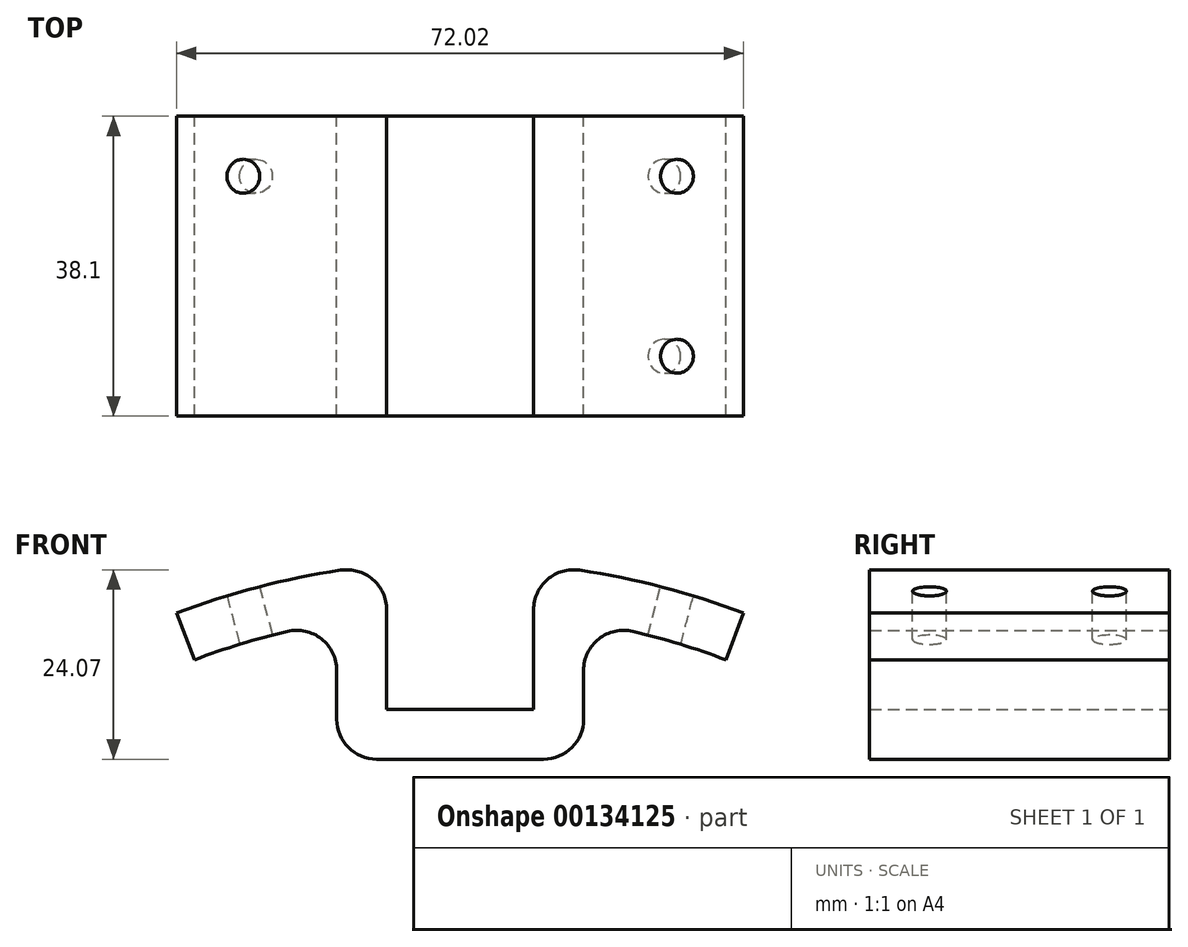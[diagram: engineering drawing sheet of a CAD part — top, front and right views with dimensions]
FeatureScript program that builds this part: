
annotation { "Feature Type Name" : "Feature", "Feature Type Description" : "" }
export const myFeature = defineFeature(function(context is Context, id is Id, definition is map)
    precondition{}
    {
        {
            var Q0;
            Q0=qCreatedBy(makeId("Front.planeOp"),FACE);
            var sketch = newSketch(context, id + "F0", { "sketchPlane" : qUnion([Q0])});
            skArc(sketch, "E0", {"start": v(-9.33, 101.17) * mm, "mid": v(-22.88, 99) * mm, "end": v(-36, 95) * mm});
            skLineSegment(sketch, "E1.bottom", {"start": v(9.33, 82.8) * mm, "end": v(-9.33, 82.8) * mm});
            skLineSegment(sketch, "E1.left", {"start": v(9.33, 82.8) * mm, "end": v(9.33, 101.17) * mm});
            skLineSegment(sketch, "E1.right", {"start": v(-9.33, 82.8) * mm, "end": v(-9.33, 101.17) * mm});
            skPoint(sketch, "E1.middle", {"position": v(0, 101.6) * mm});
            skArc(sketch, "E2", {"start": v(-15.68, 93.95) * mm, "mid": v(-24.84, 91.95) * mm, "end": v(-33.76, 89.07) * mm});
            skPoint(sketch, "E3.orphan", {"position": v(9.33, 120.4) * mm});
            skPoint(sketch, "E4.orphan", {"position": v(-9.33, 120.4) * mm});
            skLineSegment(sketch, "E5.bottom", {"start": v(15.68, 76.45) * mm, "end": v(-15.68, 76.45) * mm});
            skLineSegment(sketch, "E5.left", {"start": v(15.68, 76.45) * mm, "end": v(15.68, 93.95) * mm});
            skLineSegment(sketch, "E5.right", {"start": v(-15.68, 76.45) * mm, "end": v(-15.68, 93.95) * mm});
            skPoint(sketch, "E6.MirrorCS.end.orphan", {"position": v(27.3, 97.87) * mm});
            skPoint(sketch, "E7.end.orphan", {"position": v(-27.3, 97.87) * mm});
            skPoint(sketch, "E5.top.start.orphan", {"position": v(15.68, 126.75) * mm});
            skPoint(sketch, "E8.orphan", {"position": v(-15.68, 126.75) * mm});
            skLineSegment(sketch, "E9", {"start": v(-33.76, 89.07) * mm, "end": v(-36, 95) * mm});
            skLineSegment(sketch, "E10.MirrorCS", {"start": v(33.76, 89.07) * mm, "end": v(36, 95) * mm});
            skArc(sketch, "E11.trimOffspring", {"start": v(36, 95) * mm, "mid": v(22.88, 99) * mm, "end": v(9.33, 101.17) * mm});
            skArc(sketch, "E12.trimOffspring", {"start": v(33.76, 89.07) * mm, "mid": v(24.84, 91.95) * mm, "end": v(15.68, 93.95) * mm});
            skSolve(sketch);
        }
        {
            var Q0;
            Q0=makeQuery(id+"F0.imprint","IMPRINT",FACE,{"disambiguationData":[TD([[makeQuery(id+"F0.imprint","IMPRINT",EDGE,{"derivedFrom":sQuery(id+"F0.wireOp",EDGE,"E0")}),1.0]])]});
            extrude(context, id + "F1", {"entities" : qUnion([Q0]), "depth" : 38.1 * mm});
        }
        {
            var Q0;
            Q0=makeQuery(id+"F1.opExtrude","SWEPT_EDGE",EDGE,{"disambiguationData":[OSD([sQuery(id+"F0.wireOp",EDGE,"E0"),sQuery(id+"F0.wireOp",EDGE,"E1.right")])]});
            var Q1;
            Q1=makeQuery(id+"F1.opExtrude","SWEPT_EDGE",EDGE,{"disambiguationData":[OSD([sQuery(id+"F0.wireOp",EDGE,"E1.left"),sQuery(id+"F0.wireOp",EDGE,"E11.trimOffspring")])]});
            var Q2;
            Q2=makeQuery(id+"F1.opExtrude","SWEPT_EDGE",EDGE,{"disambiguationData":[OSD([sQuery(id+"F0.wireOp",EDGE,"E5.left"),sQuery(id+"F0.wireOp",EDGE,"E12.trimOffspring")])]});
            var Q3;
            Q3=makeQuery(id+"F1.opExtrude","SWEPT_EDGE",EDGE,{"disambiguationData":[OSD([sQuery(id+"F0.wireOp",EDGE,"E2"),sQuery(id+"F0.wireOp",EDGE,"E5.right")])]});
            var Q4;
            Q4=makeQuery(id+"F1.opExtrude","SWEPT_EDGE",EDGE,{"disambiguationData":[OSD([sQuery(id+"F0.wireOp",EDGE,"E5.bottom"),sQuery(id+"F0.wireOp",EDGE,"E5.left")])]});
            var Q5;
            Q5=makeQuery(id+"F1.opExtrude","SWEPT_EDGE",EDGE,{"disambiguationData":[OSD([sQuery(id+"F0.wireOp",EDGE,"E5.bottom"),sQuery(id+"F0.wireOp",EDGE,"E5.right")])]});
            fillet(context, id + "F2", {"entities" : qUnion([Q0, Q1, Q2, Q3, Q4, Q5]), "radius" : 5.08 * mm, "tangentPropagation" : true, "allowEdgeOverflow" : false});
        }
        {
            var Q0;
            Q0=makeQuery(id+"F1.opExtrude","SWEPT_EDGE",EDGE,{"disambiguationData":[OSD([sQuery(id+"F0.wireOp",EDGE,"E0"),sQuery(id+"F0.wireOp",EDGE,"E9")])]});
            var Q1;
            {var subQ0=sQuery(id+"F0.wireOp",EDGE,"E0");Q1=makeQuery(id+"F2.opFillet","BLEND_EDGE",EDGE,{"blendedFrom":[makeQuery(id+"F1.opExtrude","SWEPT_EDGE",EDGE,{"disambiguationData":[OSD([subQ0,sQuery(id+"F0.wireOp",EDGE,"E1.right")])]}),makeQuery(id+"F1.opExtrude","SWEPT_FACE",FACE,{"disambiguationData":[OSD([subQ0])]})],"blendedInto":[makeQuery(id+"F1.opExtrude","SWEPT_FACE",FACE,{"disambiguationData":[OSD([subQ0])]})]});}
            cPlane(context, id + "F3", {"entities" : qUnion([Q0, Q1]), "cplaneType" : CPlaneType.LINE_ANGLE, "offset" : 25.4 * mm, "angle" : 0 * degree, "width" : 152.4 * mm, "height" : 152.4 * mm});
        }
        {
            var Q0;
            Q0=qCreatedBy(id+"F3.planeOp",FACE);
            var sketch = newSketch(context, id + "F4", { "sketchPlane" : qUnion([Q0])});
            skCircle(sketch, "E13", {"center": v(-1.88, 7.62) * mm, "radius": 2.16 * mm});
            skLineSegment(sketch, "E14", {"start": v(-1.88, 0) * mm, "end": v(-10.77, 0) * mm});
            skLineSegment(sketch, "E15", {"start": v(-1.88, 38.1) * mm, "end": v(-10.77, 38.1) * mm});
            skLineSegment(sketch, "E16", {"start": v(-1.88, 38.1) * mm, "end": v(-1.88, 0) * mm});
            skCircle(sketch, "E17", {"center": v(-1.88, 30.48) * mm, "radius": 2.16 * mm});
            skLineSegment(sketch, "E18", {"start": v(-1.88, 38.1) * mm, "end": v(-1.88, 30.48) * mm});
            skSolve(sketch);
        }
        {
            var Q0;
            {var subQ0=sQuery(id+"F0.wireOp",EDGE,"E11.trimOffspring");Q0=makeQuery(id+"F2.opFillet","BLEND_EDGE",EDGE,{"blendedFrom":[makeQuery(id+"F1.opExtrude","SWEPT_EDGE",EDGE,{"disambiguationData":[OSD([sQuery(id+"F0.wireOp",EDGE,"E1.left"),subQ0])]}),makeQuery(id+"F1.opExtrude","SWEPT_FACE",FACE,{"disambiguationData":[OSD([subQ0])]})],"blendedInto":[makeQuery(id+"F1.opExtrude","SWEPT_FACE",FACE,{"disambiguationData":[OSD([subQ0])]})]});}
            var Q1;
            Q1=makeQuery(id+"F1.opExtrude","SWEPT_EDGE",EDGE,{"disambiguationData":[OSD([sQuery(id+"F0.wireOp",EDGE,"E10.MirrorCS"),sQuery(id+"F0.wireOp",EDGE,"E11.trimOffspring")])]});
            cPlane(context, id + "F5", {"entities" : qUnion([Q0, Q1]), "cplaneType" : CPlaneType.LINE_ANGLE, "offset" : 25.4 * mm, "angle" : 0 * degree, "width" : 152.4 * mm, "height" : 152.4 * mm});
        }
        {
            var Q0;
            Q0=qCreatedBy(id+"F5.planeOp",FACE);
            var sketch = newSketch(context, id + "F6", { "sketchPlane" : qUnion([Q0])});
            skCircle(sketch, "E19", {"center": v(1.88, 7.62) * mm, "radius": 2.16 * mm});
            skCircle(sketch, "E20", {"center": v(1.88, 30.48) * mm, "radius": 2.16 * mm});
            skLineSegment(sketch, "E21", {"start": v(10.77, 38.1) * mm, "end": v(1.88, 38.1) * mm});
            skLineSegment(sketch, "E22", {"start": v(1.88, 0) * mm, "end": v(10.77, 0) * mm});
            skLineSegment(sketch, "E23", {"start": v(1.88, 0) * mm, "end": v(1.88, 38.1) * mm});
            skSolve(sketch);
        }
        {
            var Q0;
            {var subQ0=sQuery(id+"F4.wireOp",EDGE,"E13");var subQ1=sQuery(id+"F4.wireOp",EDGE,"MtRigjMj-3dSd-aA1d-ol25-ydxgadoNVgCU");var subQ2=makeQuery(id+"F4.imprint","INTERSECT",VERTEX,{"disambiguationData":[OD(0.0)],"derivedFrom":[subQ1,subQ0]});Q0=makeQuery(id+"F4.imprint","IMPRINT",FACE,{"disambiguationData":[TD([[makeQuery(id+"F4.imprint","IMPRINT",EDGE,{"disambiguationData":[TD([[subQ2,1.0]])],"derivedFrom":subQ1}),1.0]])]});}
            var Q1;
            {var subQ0=sQuery(id+"F4.wireOp",EDGE,"E13");var subQ1=sQuery(id+"F4.wireOp",EDGE,"MtRigjMj-3dSd-aA1d-ol25-ydxgadoNVgCU");var subQ2=makeQuery(id+"F4.imprint","INTERSECT",VERTEX,{"disambiguationData":[OD(0.0)],"derivedFrom":[subQ1,subQ0]});Q1=makeQuery(id+"F4.imprint","IMPRINT",FACE,{"disambiguationData":[TD([[makeQuery(id+"F4.imprint","IMPRINT",EDGE,{"disambiguationData":[TD([[subQ2,1.0]])],"derivedFrom":subQ1}),-1.0]])]});}
            var Q2;
            Q2=makeQuery(id+"F4.imprint","IMPRINT",FACE,{"disambiguationData":[TD([[makeQuery(id+"F4.imprint","IMPRINT",EDGE,{"derivedFrom":sQuery(id+"F4.wireOp",EDGE,"FilW5u5A-EfiJ-iQZp-4yOM-Yht80zadNHdD")}),1.0]])]});
            var Q3;
            {var subQ0=sQuery(id+"F6.wireOp",EDGE,"AlFrU4an-jmT9-QRRX-vHQV-c8fI0KjrH0Lw");var subQ1=sQuery(id+"F6.wireOp",EDGE,"E20");var subQ2=makeQuery(id+"F6.imprint","INTERSECT",VERTEX,{"disambiguationData":[OD(0.0)],"derivedFrom":[subQ1,subQ0]});Q3=makeQuery(id+"F6.imprint","IMPRINT",FACE,{"disambiguationData":[TD([[makeQuery(id+"F6.imprint","IMPRINT",EDGE,{"disambiguationData":[TD([[subQ2,-1.0]])],"derivedFrom":subQ1}),1.0]])]});}
            var Q4;
            {var subQ0=sQuery(id+"F6.wireOp",EDGE,"AlFrU4an-jmT9-QRRX-vHQV-c8fI0KjrH0Lw");var subQ1=sQuery(id+"F6.wireOp",EDGE,"E20");var subQ2=makeQuery(id+"F6.imprint","INTERSECT",VERTEX,{"disambiguationData":[OD(0.0)],"derivedFrom":[subQ1,subQ0]});Q4=makeQuery(id+"F6.imprint","IMPRINT",FACE,{"disambiguationData":[TD([[makeQuery(id+"F6.imprint","IMPRINT",EDGE,{"disambiguationData":[TD([[subQ2,1.0]])],"derivedFrom":subQ1}),1.0]])]});}
            var Q5;
            {var subQ0=sQuery(id+"F6.wireOp",EDGE,"AlFrU4an-jmT9-QRRX-vHQV-c8fI0KjrH0Lw");var subQ1=sQuery(id+"F6.wireOp",EDGE,"E19");var subQ2=makeQuery(id+"F6.imprint","INTERSECT",VERTEX,{"disambiguationData":[OD(0.0)],"derivedFrom":[subQ1,subQ0]});Q5=makeQuery(id+"F6.imprint","IMPRINT",FACE,{"disambiguationData":[TD([[makeQuery(id+"F6.imprint","IMPRINT",EDGE,{"disambiguationData":[TD([[subQ2,-1.0]])],"derivedFrom":subQ1}),1.0]])]});}
            var Q6;
            {var subQ0=sQuery(id+"F6.wireOp",EDGE,"AlFrU4an-jmT9-QRRX-vHQV-c8fI0KjrH0Lw");var subQ1=sQuery(id+"F6.wireOp",EDGE,"E19");var subQ2=makeQuery(id+"F6.imprint","INTERSECT",VERTEX,{"disambiguationData":[OD(0.0)],"derivedFrom":[subQ1,subQ0]});Q6=makeQuery(id+"F6.imprint","IMPRINT",FACE,{"disambiguationData":[TD([[makeQuery(id+"F6.imprint","IMPRINT",EDGE,{"disambiguationData":[TD([[subQ2,1.0]])],"derivedFrom":subQ1}),1.0]])]});}
            extrude(context, id + "F7", {"entities" : qUnion([Q0, Q1, Q2, Q3, Q4, Q5, Q6]), "operationType" : NewBodyOperationType.REMOVE, "endBound" : BoundingType.SYMMETRIC, "depth" : 25.4 * mm});
        }
        {
            var Q0;
            {var subQ0=sQuery(id+"F4.wireOp",EDGE,"E18");var subQ1=sQuery(id+"F4.wireOp",EDGE,"E16");var subQ2=makeQuery(id+"F4.imprint","INTERSECT",VERTEX,{"derivedFrom":[subQ1,subQ0]});Q0=makeQuery(id+"F4.imprint","IMPRINT",FACE,{"disambiguationData":[TD([[makeQuery(id+"F4.imprint","IMPRINT",EDGE,{"disambiguationData":[TD([[subQ2,-1.0]])],"derivedFrom":subQ1}),-1.0]])]});}
            var Q1;
            {var subQ0=sQuery(id+"F4.wireOp",EDGE,"E18");var subQ1=sQuery(id+"F4.wireOp",EDGE,"E16");var subQ2=makeQuery(id+"F4.imprint","INTERSECT",VERTEX,{"derivedFrom":[subQ1,subQ0]});Q1=makeQuery(id+"F4.imprint","IMPRINT",FACE,{"disambiguationData":[TD([[makeQuery(id+"F4.imprint","IMPRINT",EDGE,{"disambiguationData":[TD([[subQ2,-1.0]])],"derivedFrom":subQ1}),1.0]])]});}
            var Q2;
            {var subQ0=sQuery(id+"F4.wireOp",EDGE,"E16");var subQ1=sQuery(id+"F4.wireOp",EDGE,"E13");var subQ2=makeQuery(id+"F4.imprint","INTERSECT",VERTEX,{"disambiguationData":[OD(0.0)],"derivedFrom":[subQ1,subQ0]});Q2=makeQuery(id+"F4.imprint","IMPRINT",FACE,{"disambiguationData":[TD([[makeQuery(id+"F4.imprint","IMPRINT",EDGE,{"disambiguationData":[TD([[subQ2,1.0]])],"derivedFrom":subQ1}),1.0]])]});}
            var Q3;
            {var subQ0=sQuery(id+"F4.wireOp",EDGE,"E16");var subQ1=sQuery(id+"F4.wireOp",EDGE,"E13");var subQ2=makeQuery(id+"F4.imprint","INTERSECT",VERTEX,{"disambiguationData":[OD(0.0)],"derivedFrom":[subQ1,subQ0]});Q3=makeQuery(id+"F4.imprint","IMPRINT",FACE,{"disambiguationData":[TD([[makeQuery(id+"F4.imprint","IMPRINT",EDGE,{"disambiguationData":[TD([[subQ2,-1.0]])],"derivedFrom":subQ1}),1.0]])]});}
            extrude(context, id + "F8", {"entities" : qUnion([Q0, Q1, Q2, Q3]), "operationType" : NewBodyOperationType.REMOVE, "endBound" : BoundingType.SYMMETRIC, "oppositeDirection" : true, "depth" : 25.4 * mm});
        }
    });
